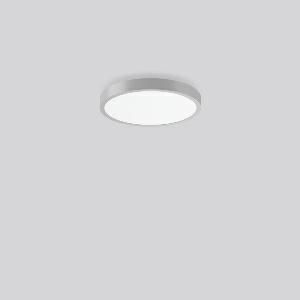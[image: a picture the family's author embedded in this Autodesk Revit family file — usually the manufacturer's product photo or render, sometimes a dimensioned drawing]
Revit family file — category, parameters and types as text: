
# Revit family: triona_round_a_312420_004_2_76_d1ae
name_source: partatom
category: Lighting Fixtures
units: mm (PartAtom-declared; Revit-internal decimal feet)

## family parameters
Cut with Voids When Loaded = No
Host = Face
Light Source = No
Part Type = Normal
Room Calculation Point = No
Round Connector Dimension = Use Diameter
Shared = No

## types (1)
- TuneableWhite 846 (1 x LED Modul 846, 3050 lm, 4600)
    Apparent Load = 38 VA
    CIE Flux Codes = 48 79 96 82 100
    Color Rendering = 80
    Color Temperature = 4600
    Default Elevation = 1800 mm
    Description = Series: TRIONA round
Decorative round LED surface-mounted luminaire. Flat, seamless frame: aluminium extrusion profile, powder coated. Cover made of sheet steel, powder-coated. Direct light emission through a diffuser plastic opal. Indirect light emission through a flush diffuser made of satin-finish plastic. Lightguide and diffuser made of non-yellowing plastic (PMMA). Lateral light emission (RZB SIDELITE technology) for above-average homogeneous light distribution. Direct 70%, indirect 30% light emission. Tunable white versions, dynamically adjustable from 2700 K to 6500 K. Suitable for Ceiling mounting, Wall (surface). Tool-free mounting via bayonet connection. Electronic ballast included. Very easy installation thanks to Plug+Play connection. Ideal for use as part of the Human Centric Lighting concept in connection with RZB light management systems. 
Colour: silver, matt (approx. RAL 9006)
Diameter: 461 mm
Height: 88 mm
Lamp: LED
Socket: without socket
Colour temperature: 2700K - 6500K
Colour rendering index (CRI): 80
System power: 38 W
Rated luminous flux: 3050 lm
Luminous efficiency: 80 lm/W
System power 2: 39 W
Rated luminous flux 2: 2900 lm
Luminous efficiency 2: 74 lm/W
System power 3: 39 W
Rated luminous flux 3: 2950 lm
Luminous efficiency 3: 76 lm/W
Control gear: Converter, dimmable, DALI
Protection class: I
Type of protection: IP 20
    Height = 88 mm
    Lamp = 1 x LED Modul 846
    Lamp Light Flux = 3050 lm
    Lamp count = 1
    Length = 461 mm
    Lifetime = 50000 h
    Luminous efficacy = 80 lm/W
    Manufacturer = RZB
    ModVariant = No
    Model = 312420.004.2.76
    Mounting Place = Ceiling
    Mounting Type = Surface mounted
    Number of Poles = 1
    OnlyDefault = Yes
    Power Factor = 1
    Product Name = TRIONA round A
    Product group = Surface mounted modular luminaires
    ProductGroupID = 306
    Protection Class = Protection class I
    Protection Degree = IP 20
    RLX_Detail_Level = 1
    RLX_Emergency_Light_Flux = 0 lm
    RLX_Emergency_Type = 0
    RLX_Emergency_Type_DB = No
    RlxData = <blob elided: 38809 chars, md5=1282bcf2>
    Socket = socket
    Standby Power = 0 W
    System Light Flux = 3050 lm
    System Power = 38 W
    Type Comments = TuneableWhite 846
    Type Image = 312420.004.jpg
    URL = http://relux.com
    VarID = tuneablewhite_846
    Voltage = 230 V
    Voltage Range = 220-240 V
    Weight = 0.00 kg
    Width = 0 mm  [stored 0 ft]

note: [stored X ft] marks values corroborated as IEEE doubles in the binary element streams (Revit-internal decimal feet)

## geometry (parser evidence)
native form markers: Blend x4, Sweep x12
no freeform markers — native parametric forms only
